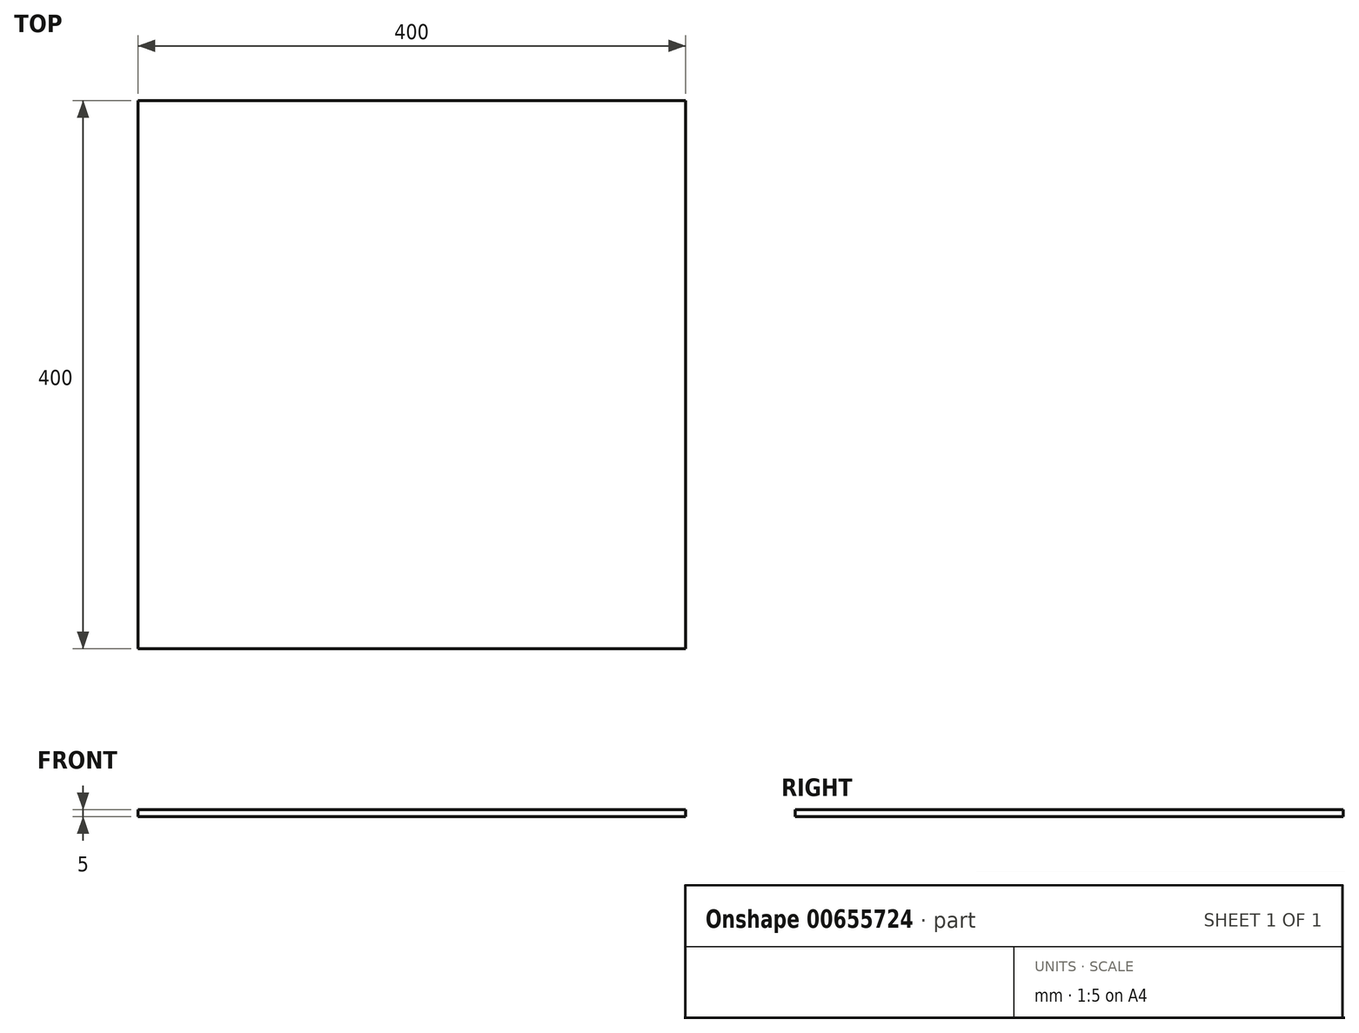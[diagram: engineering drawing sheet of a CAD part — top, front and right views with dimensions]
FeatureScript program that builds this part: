
annotation { "Feature Type Name" : "Feature", "Feature Type Description" : "" }
export const myFeature = defineFeature(function(context is Context, id is Id, definition is map)
    precondition{}
    {
        {
            var Q0;
            Q0=qCreatedBy(makeId("Top.planeOp"),FACE);
            var sketch = newSketch(context, id + "F0", { "sketchPlane" : qUnion([Q0])});
            skLineSegment(sketch, "E0.bottom", {"start": v(-75.07, -58.35) * mm, "end": v(324.93, -58.35) * mm});
            skLineSegment(sketch, "E0.top", {"start": v(-75.07, 341.65) * mm, "end": v(324.93, 341.65) * mm});
            skLineSegment(sketch, "E0.left", {"start": v(-75.07, -58.35) * mm, "end": v(-75.07, 341.65) * mm});
            skLineSegment(sketch, "E0.right", {"start": v(324.93, -58.35) * mm, "end": v(324.93, 341.65) * mm});
            skSolve(sketch);
        }
        {
            var Q0;
            Q0 = qSketchRegion(id + "F0", true);
            extrude(context, id + "F1", {"entities" : qUnion([Q0]), "depth" : 5 * mm, "offsetDistance" : 25 * mm});
        }
    });
